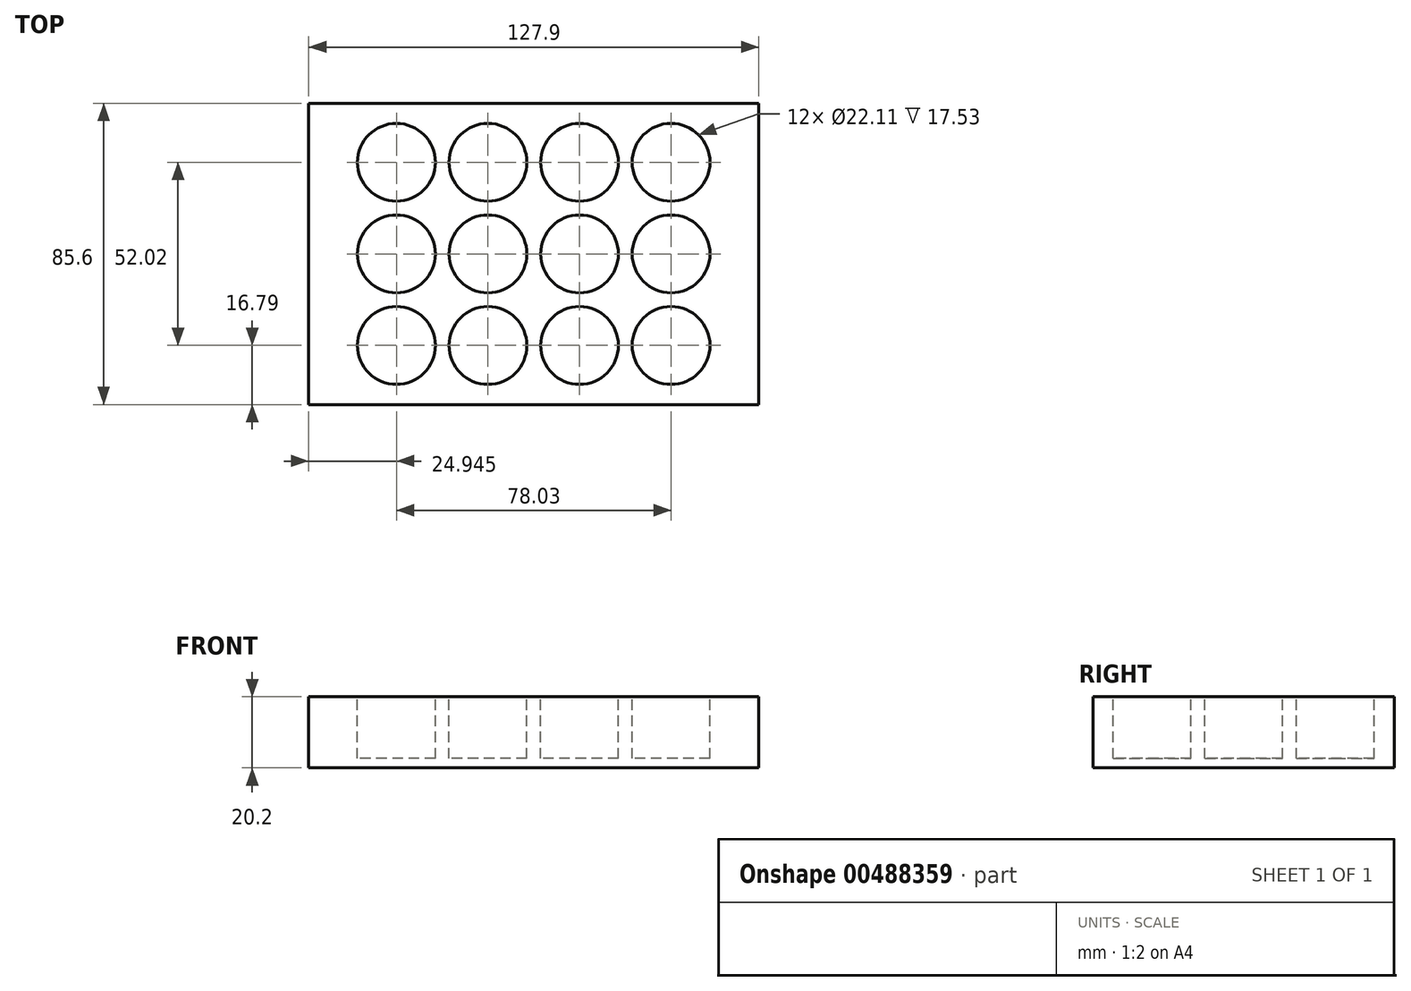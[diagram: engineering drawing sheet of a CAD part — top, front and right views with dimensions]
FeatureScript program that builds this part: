
annotation { "Feature Type Name" : "Feature", "Feature Type Description" : "" }
export const myFeature = defineFeature(function(context is Context, id is Id, definition is map)
    precondition{}
    {
        {
            var Q0;
            Q0=qCreatedBy(makeId("Top.planeOp"),FACE);
            var sketch = newSketch(context, id + "F0", { "sketchPlane" : qUnion([Q0])});
            skLineSegment(sketch, "E0.bottom", {"start": v(63.95, 42.8) * mm, "end": v(-63.95, 42.8) * mm});
            skLineSegment(sketch, "E0.top", {"start": v(63.95, -42.8) * mm, "end": v(-63.95, -42.8) * mm});
            skLineSegment(sketch, "E0.left", {"start": v(63.95, 42.8) * mm, "end": v(63.95, -42.8) * mm});
            skLineSegment(sketch, "E0.right", {"start": v(-63.95, 42.8) * mm, "end": v(-63.95, -42.8) * mm});
            skPoint(sketch, "E0.middle", {"position": v(0, 0) * mm});
            skSolve(sketch);
        }
        {
            var Q0;
            Q0=qSketchRegion(id+"F0",true);
            extrude(context, id + "F1", {"entities" : qUnion([Q0]), "depth" : 20.2 * mm});
        }
        {
            var Q0;
            Q0=makeQuery(id+"F1.opExtrude","CAP_FACE",FACE,{"disambiguationData":[OSD([sQuery(id+"F0.wireOp",EDGE,"E0.bottom"),sQuery(id+"F0.wireOp",EDGE,"E0.top"),sQuery(id+"F0.wireOp",EDGE,"E0.left"),sQuery(id+"F0.wireOp",EDGE,"E0.right")])],"isStart":false});
            var sketch = newSketch(context, id + "F2", { "sketchPlane" : qUnion([Q0])});
            skLineSegment(sketch, "E1.bottom", {"start": v(63.95, 42.8) * mm, "end": v(-63.95, 42.8) * mm});
            skLineSegment(sketch, "E1.top", {"start": v(63.95, -42.8) * mm, "end": v(-63.95, -42.8) * mm});
            skLineSegment(sketch, "E1.left", {"start": v(63.95, 42.8) * mm, "end": v(63.95, -42.8) * mm});
            skLineSegment(sketch, "E1.right", {"start": v(-63.95, 42.8) * mm, "end": v(-63.95, -42.8) * mm});
            skPoint(sketch, "E1.middle", {"position": v(0, 0) * mm});
            skLineSegment(sketch, "E2", {"start": v(-63.95, -42.8) * mm, "end": v(-39, -42.8) * mm});
            skLineSegment(sketch, "E3", {"start": v(-63.95, 42.8) * mm, "end": v(-63.95, 26) * mm});
            skLineSegment(sketch, "E4", {"start": v(-39, -42.8) * mm, "end": v(-13, -42.8) * mm});
            skLineSegment(sketch, "E5", {"start": v(-13, -42.8) * mm, "end": v(13.01, -42.8) * mm});
            skLineSegment(sketch, "E6", {"start": v(13.01, -42.8) * mm, "end": v(39.02, -42.8) * mm});
            skLineSegment(sketch, "E7", {"start": v(-63.95, 26) * mm, "end": v(-63.95, 0) * mm});
            skLineSegment(sketch, "E8", {"start": v(-63.95, 0) * mm, "end": v(-63.95, -26.01) * mm});
            skLineSegment(sketch, "E9", {"start": v(-63.95, 26) * mm, "end": v(63.95, 26.01) * mm});
            skLineSegment(sketch, "E10", {"start": v(63.95, 26.01) * mm, "end": v(63.95, 42.8) * mm});
            skLineSegment(sketch, "E11", {"start": v(-63.95, 0) * mm, "end": v(63.95, 0) * mm});
            skLineSegment(sketch, "E12", {"start": v(63.95, 0) * mm, "end": v(63.95, 26.01) * mm});
            skLineSegment(sketch, "E13", {"start": v(-63.95, -26.01) * mm, "end": v(63.95, -26.01) * mm});
            skLineSegment(sketch, "E14", {"start": v(63.95, -26.01) * mm, "end": v(63.95, 0) * mm});
            skLineSegment(sketch, "E15", {"start": v(-39, -42.8) * mm, "end": v(-39, 42.8) * mm});
            skLineSegment(sketch, "E16", {"start": v(-39, 42.8) * mm, "end": v(-63.95, 42.8) * mm});
            skLineSegment(sketch, "E17", {"start": v(-13, -42.8) * mm, "end": v(-13, 42.8) * mm});
            skLineSegment(sketch, "E18", {"start": v(-13, 42.8) * mm, "end": v(-39, 42.8) * mm});
            skLineSegment(sketch, "E19", {"start": v(13.01, -42.8) * mm, "end": v(13.01, 42.8) * mm});
            skLineSegment(sketch, "E20", {"start": v(13.01, 42.8) * mm, "end": v(-13, 42.8) * mm});
            skLineSegment(sketch, "E21", {"start": v(39.02, -42.8) * mm, "end": v(39.02, 42.8) * mm});
            skLineSegment(sketch, "E22", {"start": v(39.02, 42.8) * mm, "end": v(13.01, 42.8) * mm});
            skCircle(sketch, "E23", {"center": v(-39, 26) * mm, "radius": 11.05 * mm});
            skCircle(sketch, "E24", {"center": v(-13, 26) * mm, "radius": 11.05 * mm});
            skCircle(sketch, "E25", {"center": v(13.01, 26) * mm, "radius": 11.05 * mm});
            skCircle(sketch, "E26", {"center": v(39.02, 26.01) * mm, "radius": 11.05 * mm});
            skCircle(sketch, "E27", {"center": v(-13, 0) * mm, "radius": 11.05 * mm});
            skCircle(sketch, "E28", {"center": v(13.01, 0) * mm, "radius": 11.05 * mm});
            skCircle(sketch, "E29", {"center": v(39.02, 0) * mm, "radius": 11.05 * mm});
            skCircle(sketch, "E30", {"center": v(-13, -26.01) * mm, "radius": 11.05 * mm});
            skCircle(sketch, "E31", {"center": v(13.01, -26.01) * mm, "radius": 11.05 * mm});
            skCircle(sketch, "E32", {"center": v(39.02, -26.01) * mm, "radius": 11.05 * mm});
            skCircle(sketch, "E33", {"center": v(-39, 0) * mm, "radius": 11.05 * mm});
            skCircle(sketch, "E34", {"center": v(-39, -26.01) * mm, "radius": 11.05 * mm});
            skLineSegment(sketch, "E35", {"start": v(39.02, -42.8) * mm, "end": v(63.95, -42.8) * mm});
            skLineSegment(sketch, "E36", {"start": v(63.95, -26.01) * mm, "end": v(63.95, -42.8) * mm});
            skSolve(sketch);
        }
        {
            var Q0;
            {var subQ0=sQuery(id+"F2.wireOp",EDGE,"E23");var subQ1=sQuery(id+"F2.wireOp",EDGE,"E9");var subQ2=makeQuery(id+"F2.imprint","INTERSECT",VERTEX,{"disambiguationData":[OD(0.0)],"derivedFrom":[subQ1,subQ0]});Q0=makeQuery(id+"F2.imprint","IMPRINT",FACE,{"disambiguationData":[TD([[makeQuery(id+"F2.imprint","IMPRINT",EDGE,{"disambiguationData":[TD([[subQ2,-1.0]])],"derivedFrom":subQ1}),1.0]])]});}
            var Q1;
            {var subQ0=sQuery(id+"F2.wireOp",EDGE,"E15");var subQ1=sQuery(id+"F2.wireOp",EDGE,"E9");var subQ2=makeQuery(id+"F2.imprint","INTERSECT",VERTEX,{"derivedFrom":[subQ1,subQ0]});Q1=makeQuery(id+"F2.imprint","IMPRINT",FACE,{"disambiguationData":[TD([[makeQuery(id+"F2.imprint","IMPRINT",EDGE,{"disambiguationData":[TD([[subQ2,-1.0]])],"derivedFrom":subQ1}),1.0]])]});}
            var Q2;
            {var subQ0=sQuery(id+"F2.wireOp",EDGE,"E15");var subQ1=sQuery(id+"F2.wireOp",EDGE,"E9");var subQ2=makeQuery(id+"F2.imprint","INTERSECT",VERTEX,{"derivedFrom":[subQ1,subQ0]});Q2=makeQuery(id+"F2.imprint","IMPRINT",FACE,{"disambiguationData":[TD([[makeQuery(id+"F2.imprint","IMPRINT",EDGE,{"disambiguationData":[TD([[subQ2,-1.0]])],"derivedFrom":subQ1}),-1.0]])]});}
            var Q3;
            {var subQ0=sQuery(id+"F2.wireOp",EDGE,"E23");var subQ1=sQuery(id+"F2.wireOp",EDGE,"E9");var subQ2=makeQuery(id+"F2.imprint","INTERSECT",VERTEX,{"disambiguationData":[OD(0.0)],"derivedFrom":[subQ1,subQ0]});Q3=makeQuery(id+"F2.imprint","IMPRINT",FACE,{"disambiguationData":[TD([[makeQuery(id+"F2.imprint","IMPRINT",EDGE,{"disambiguationData":[TD([[subQ2,-1.0]])],"derivedFrom":subQ1}),-1.0]])]});}
            var Q4;
            {var subQ0=sQuery(id+"F2.wireOp",EDGE,"E33");var subQ1=sQuery(id+"F2.wireOp",EDGE,"E11");var subQ2=makeQuery(id+"F2.imprint","INTERSECT",VERTEX,{"disambiguationData":[OD(0.0)],"derivedFrom":[subQ1,subQ0]});Q4=makeQuery(id+"F2.imprint","IMPRINT",FACE,{"disambiguationData":[TD([[makeQuery(id+"F2.imprint","IMPRINT",EDGE,{"disambiguationData":[TD([[subQ2,-1.0]])],"derivedFrom":subQ1}),1.0]])]});}
            var Q5;
            {var subQ0=sQuery(id+"F2.wireOp",EDGE,"E15");var subQ1=sQuery(id+"F2.wireOp",EDGE,"E11");var subQ2=makeQuery(id+"F2.imprint","INTERSECT",VERTEX,{"derivedFrom":[subQ1,subQ0]});Q5=makeQuery(id+"F2.imprint","IMPRINT",FACE,{"disambiguationData":[TD([[makeQuery(id+"F2.imprint","IMPRINT",EDGE,{"disambiguationData":[TD([[subQ2,-1.0]])],"derivedFrom":subQ1}),1.0]])]});}
            var Q6;
            {var subQ0=sQuery(id+"F2.wireOp",EDGE,"E33");var subQ1=sQuery(id+"F2.wireOp",EDGE,"E11");var subQ2=makeQuery(id+"F2.imprint","INTERSECT",VERTEX,{"disambiguationData":[OD(0.0)],"derivedFrom":[subQ1,subQ0]});Q6=makeQuery(id+"F2.imprint","IMPRINT",FACE,{"disambiguationData":[TD([[makeQuery(id+"F2.imprint","IMPRINT",EDGE,{"disambiguationData":[TD([[subQ2,-1.0]])],"derivedFrom":subQ1}),-1.0]])]});}
            var Q7;
            {var subQ0=sQuery(id+"F2.wireOp",EDGE,"E15");var subQ1=sQuery(id+"F2.wireOp",EDGE,"E11");var subQ2=makeQuery(id+"F2.imprint","INTERSECT",VERTEX,{"derivedFrom":[subQ1,subQ0]});Q7=makeQuery(id+"F2.imprint","IMPRINT",FACE,{"disambiguationData":[TD([[makeQuery(id+"F2.imprint","IMPRINT",EDGE,{"disambiguationData":[TD([[subQ2,-1.0]])],"derivedFrom":subQ1}),-1.0]])]});}
            var Q8;
            {var subQ0=sQuery(id+"F2.wireOp",EDGE,"E15");var subQ1=sQuery(id+"F2.wireOp",EDGE,"E13");var subQ2=makeQuery(id+"F2.imprint","INTERSECT",VERTEX,{"derivedFrom":[subQ1,subQ0]});Q8=makeQuery(id+"F2.imprint","IMPRINT",FACE,{"disambiguationData":[TD([[makeQuery(id+"F2.imprint","IMPRINT",EDGE,{"disambiguationData":[TD([[subQ2,-1.0]])],"derivedFrom":subQ1}),1.0]])]});}
            var Q9;
            {var subQ0=sQuery(id+"F2.wireOp",EDGE,"E34");var subQ1=sQuery(id+"F2.wireOp",EDGE,"E13");var subQ2=makeQuery(id+"F2.imprint","INTERSECT",VERTEX,{"disambiguationData":[OD(0.0)],"derivedFrom":[subQ1,subQ0]});Q9=makeQuery(id+"F2.imprint","IMPRINT",FACE,{"disambiguationData":[TD([[makeQuery(id+"F2.imprint","IMPRINT",EDGE,{"disambiguationData":[TD([[subQ2,-1.0]])],"derivedFrom":subQ1}),1.0]])]});}
            var Q10;
            {var subQ0=sQuery(id+"F2.wireOp",EDGE,"E34");var subQ1=sQuery(id+"F2.wireOp",EDGE,"E13");var subQ2=makeQuery(id+"F2.imprint","INTERSECT",VERTEX,{"disambiguationData":[OD(0.0)],"derivedFrom":[subQ1,subQ0]});Q10=makeQuery(id+"F2.imprint","IMPRINT",FACE,{"disambiguationData":[TD([[makeQuery(id+"F2.imprint","IMPRINT",EDGE,{"disambiguationData":[TD([[subQ2,-1.0]])],"derivedFrom":subQ1}),-1.0]])]});}
            var Q11;
            {var subQ0=sQuery(id+"F2.wireOp",EDGE,"E15");var subQ1=sQuery(id+"F2.wireOp",EDGE,"E13");var subQ2=makeQuery(id+"F2.imprint","INTERSECT",VERTEX,{"derivedFrom":[subQ1,subQ0]});Q11=makeQuery(id+"F2.imprint","IMPRINT",FACE,{"disambiguationData":[TD([[makeQuery(id+"F2.imprint","IMPRINT",EDGE,{"disambiguationData":[TD([[subQ2,-1.0]])],"derivedFrom":subQ1}),-1.0]])]});}
            var Q12;
            {var subQ0=sQuery(id+"F2.wireOp",EDGE,"E30");var subQ1=sQuery(id+"F2.wireOp",EDGE,"E13");var subQ2=makeQuery(id+"F2.imprint","INTERSECT",VERTEX,{"disambiguationData":[OD(0.0)],"derivedFrom":[subQ1,subQ0]});Q12=makeQuery(id+"F2.imprint","IMPRINT",FACE,{"disambiguationData":[TD([[makeQuery(id+"F2.imprint","IMPRINT",EDGE,{"disambiguationData":[TD([[subQ2,-1.0]])],"derivedFrom":subQ1}),-1.0]])]});}
            var Q13;
            {var subQ0=sQuery(id+"F2.wireOp",EDGE,"E17");var subQ1=sQuery(id+"F2.wireOp",EDGE,"E13");var subQ2=makeQuery(id+"F2.imprint","INTERSECT",VERTEX,{"derivedFrom":[subQ1,subQ0]});Q13=makeQuery(id+"F2.imprint","IMPRINT",FACE,{"disambiguationData":[TD([[makeQuery(id+"F2.imprint","IMPRINT",EDGE,{"disambiguationData":[TD([[subQ2,-1.0]])],"derivedFrom":subQ1}),-1.0]])]});}
            var Q14;
            {var subQ0=sQuery(id+"F2.wireOp",EDGE,"E17");var subQ1=sQuery(id+"F2.wireOp",EDGE,"E13");var subQ2=makeQuery(id+"F2.imprint","INTERSECT",VERTEX,{"derivedFrom":[subQ1,subQ0]});Q14=makeQuery(id+"F2.imprint","IMPRINT",FACE,{"disambiguationData":[TD([[makeQuery(id+"F2.imprint","IMPRINT",EDGE,{"disambiguationData":[TD([[subQ2,-1.0]])],"derivedFrom":subQ1}),1.0]])]});}
            var Q15;
            {var subQ0=sQuery(id+"F2.wireOp",EDGE,"E30");var subQ1=sQuery(id+"F2.wireOp",EDGE,"E13");var subQ2=makeQuery(id+"F2.imprint","INTERSECT",VERTEX,{"disambiguationData":[OD(0.0)],"derivedFrom":[subQ1,subQ0]});Q15=makeQuery(id+"F2.imprint","IMPRINT",FACE,{"disambiguationData":[TD([[makeQuery(id+"F2.imprint","IMPRINT",EDGE,{"disambiguationData":[TD([[subQ2,-1.0]])],"derivedFrom":subQ1}),1.0]])]});}
            var Q16;
            {var subQ0=sQuery(id+"F2.wireOp",EDGE,"E27");var subQ1=sQuery(id+"F2.wireOp",EDGE,"E11");var subQ2=makeQuery(id+"F2.imprint","INTERSECT",VERTEX,{"disambiguationData":[OD(0.0)],"derivedFrom":[subQ1,subQ0]});Q16=makeQuery(id+"F2.imprint","IMPRINT",FACE,{"disambiguationData":[TD([[makeQuery(id+"F2.imprint","IMPRINT",EDGE,{"disambiguationData":[TD([[subQ2,-1.0]])],"derivedFrom":subQ1}),-1.0]])]});}
            var Q17;
            {var subQ0=sQuery(id+"F2.wireOp",EDGE,"E17");var subQ1=sQuery(id+"F2.wireOp",EDGE,"E11");var subQ2=makeQuery(id+"F2.imprint","INTERSECT",VERTEX,{"derivedFrom":[subQ1,subQ0]});Q17=makeQuery(id+"F2.imprint","IMPRINT",FACE,{"disambiguationData":[TD([[makeQuery(id+"F2.imprint","IMPRINT",EDGE,{"disambiguationData":[TD([[subQ2,-1.0]])],"derivedFrom":subQ1}),-1.0]])]});}
            var Q18;
            {var subQ0=sQuery(id+"F2.wireOp",EDGE,"E17");var subQ1=sQuery(id+"F2.wireOp",EDGE,"E11");var subQ2=makeQuery(id+"F2.imprint","INTERSECT",VERTEX,{"derivedFrom":[subQ1,subQ0]});Q18=makeQuery(id+"F2.imprint","IMPRINT",FACE,{"disambiguationData":[TD([[makeQuery(id+"F2.imprint","IMPRINT",EDGE,{"disambiguationData":[TD([[subQ2,-1.0]])],"derivedFrom":subQ1}),1.0]])]});}
            var Q19;
            {var subQ0=sQuery(id+"F2.wireOp",EDGE,"E27");var subQ1=sQuery(id+"F2.wireOp",EDGE,"E11");var subQ2=makeQuery(id+"F2.imprint","INTERSECT",VERTEX,{"disambiguationData":[OD(0.0)],"derivedFrom":[subQ1,subQ0]});Q19=makeQuery(id+"F2.imprint","IMPRINT",FACE,{"disambiguationData":[TD([[makeQuery(id+"F2.imprint","IMPRINT",EDGE,{"disambiguationData":[TD([[subQ2,-1.0]])],"derivedFrom":subQ1}),1.0]])]});}
            var Q20;
            {var subQ0=sQuery(id+"F2.wireOp",EDGE,"E24");var subQ1=sQuery(id+"F2.wireOp",EDGE,"E9");var subQ2=makeQuery(id+"F2.imprint","INTERSECT",VERTEX,{"disambiguationData":[OD(0.0)],"derivedFrom":[subQ1,subQ0]});Q20=makeQuery(id+"F2.imprint","IMPRINT",FACE,{"disambiguationData":[TD([[makeQuery(id+"F2.imprint","IMPRINT",EDGE,{"disambiguationData":[TD([[subQ2,-1.0]])],"derivedFrom":subQ1}),-1.0]])]});}
            var Q21;
            {var subQ0=sQuery(id+"F2.wireOp",EDGE,"E17");var subQ1=sQuery(id+"F2.wireOp",EDGE,"E9");var subQ2=makeQuery(id+"F2.imprint","INTERSECT",VERTEX,{"derivedFrom":[subQ1,subQ0]});Q21=makeQuery(id+"F2.imprint","IMPRINT",FACE,{"disambiguationData":[TD([[makeQuery(id+"F2.imprint","IMPRINT",EDGE,{"disambiguationData":[TD([[subQ2,-1.0]])],"derivedFrom":subQ1}),-1.0]])]});}
            var Q22;
            {var subQ0=sQuery(id+"F2.wireOp",EDGE,"E17");var subQ1=sQuery(id+"F2.wireOp",EDGE,"E9");var subQ2=makeQuery(id+"F2.imprint","INTERSECT",VERTEX,{"derivedFrom":[subQ1,subQ0]});Q22=makeQuery(id+"F2.imprint","IMPRINT",FACE,{"disambiguationData":[TD([[makeQuery(id+"F2.imprint","IMPRINT",EDGE,{"disambiguationData":[TD([[subQ2,-1.0]])],"derivedFrom":subQ1}),1.0]])]});}
            var Q23;
            {var subQ0=sQuery(id+"F2.wireOp",EDGE,"E24");var subQ1=sQuery(id+"F2.wireOp",EDGE,"E9");var subQ2=makeQuery(id+"F2.imprint","INTERSECT",VERTEX,{"disambiguationData":[OD(0.0)],"derivedFrom":[subQ1,subQ0]});Q23=makeQuery(id+"F2.imprint","IMPRINT",FACE,{"disambiguationData":[TD([[makeQuery(id+"F2.imprint","IMPRINT",EDGE,{"disambiguationData":[TD([[subQ2,-1.0]])],"derivedFrom":subQ1}),1.0]])]});}
            var Q24;
            {var subQ0=sQuery(id+"F2.wireOp",EDGE,"E25");var subQ1=sQuery(id+"F2.wireOp",EDGE,"E9");var subQ2=makeQuery(id+"F2.imprint","INTERSECT",VERTEX,{"disambiguationData":[OD(0.0)],"derivedFrom":[subQ1,subQ0]});Q24=makeQuery(id+"F2.imprint","IMPRINT",FACE,{"disambiguationData":[TD([[makeQuery(id+"F2.imprint","IMPRINT",EDGE,{"disambiguationData":[TD([[subQ2,-1.0]])],"derivedFrom":subQ1}),1.0]])]});}
            var Q25;
            {var subQ0=sQuery(id+"F2.wireOp",EDGE,"E19");var subQ1=sQuery(id+"F2.wireOp",EDGE,"E9");var subQ2=makeQuery(id+"F2.imprint","INTERSECT",VERTEX,{"derivedFrom":[subQ1,subQ0]});Q25=makeQuery(id+"F2.imprint","IMPRINT",FACE,{"disambiguationData":[TD([[makeQuery(id+"F2.imprint","IMPRINT",EDGE,{"disambiguationData":[TD([[subQ2,-1.0]])],"derivedFrom":subQ1}),1.0]])]});}
            var Q26;
            {var subQ0=sQuery(id+"F2.wireOp",EDGE,"E19");var subQ1=sQuery(id+"F2.wireOp",EDGE,"E9");var subQ2=makeQuery(id+"F2.imprint","INTERSECT",VERTEX,{"derivedFrom":[subQ1,subQ0]});Q26=makeQuery(id+"F2.imprint","IMPRINT",FACE,{"disambiguationData":[TD([[makeQuery(id+"F2.imprint","IMPRINT",EDGE,{"disambiguationData":[TD([[subQ2,-1.0]])],"derivedFrom":subQ1}),-1.0]])]});}
            var Q27;
            {var subQ0=sQuery(id+"F2.wireOp",EDGE,"E25");var subQ1=sQuery(id+"F2.wireOp",EDGE,"E9");var subQ2=makeQuery(id+"F2.imprint","INTERSECT",VERTEX,{"disambiguationData":[OD(0.0)],"derivedFrom":[subQ1,subQ0]});Q27=makeQuery(id+"F2.imprint","IMPRINT",FACE,{"disambiguationData":[TD([[makeQuery(id+"F2.imprint","IMPRINT",EDGE,{"disambiguationData":[TD([[subQ2,-1.0]])],"derivedFrom":subQ1}),-1.0]])]});}
            var Q28;
            {var subQ0=sQuery(id+"F2.wireOp",EDGE,"E28");var subQ1=sQuery(id+"F2.wireOp",EDGE,"E11");var subQ2=makeQuery(id+"F2.imprint","INTERSECT",VERTEX,{"disambiguationData":[OD(0.0)],"derivedFrom":[subQ1,subQ0]});Q28=makeQuery(id+"F2.imprint","IMPRINT",FACE,{"disambiguationData":[TD([[makeQuery(id+"F2.imprint","IMPRINT",EDGE,{"disambiguationData":[TD([[subQ2,-1.0]])],"derivedFrom":subQ1}),1.0]])]});}
            var Q29;
            {var subQ0=sQuery(id+"F2.wireOp",EDGE,"E19");var subQ1=sQuery(id+"F2.wireOp",EDGE,"E11");var subQ2=makeQuery(id+"F2.imprint","INTERSECT",VERTEX,{"derivedFrom":[subQ1,subQ0]});Q29=makeQuery(id+"F2.imprint","IMPRINT",FACE,{"disambiguationData":[TD([[makeQuery(id+"F2.imprint","IMPRINT",EDGE,{"disambiguationData":[TD([[subQ2,-1.0]])],"derivedFrom":subQ1}),1.0]])]});}
            var Q30;
            {var subQ0=sQuery(id+"F2.wireOp",EDGE,"E28");var subQ1=sQuery(id+"F2.wireOp",EDGE,"E11");var subQ2=makeQuery(id+"F2.imprint","INTERSECT",VERTEX,{"disambiguationData":[OD(0.0)],"derivedFrom":[subQ1,subQ0]});Q30=makeQuery(id+"F2.imprint","IMPRINT",FACE,{"disambiguationData":[TD([[makeQuery(id+"F2.imprint","IMPRINT",EDGE,{"disambiguationData":[TD([[subQ2,-1.0]])],"derivedFrom":subQ1}),-1.0]])]});}
            var Q31;
            {var subQ0=sQuery(id+"F2.wireOp",EDGE,"E19");var subQ1=sQuery(id+"F2.wireOp",EDGE,"E11");var subQ2=makeQuery(id+"F2.imprint","INTERSECT",VERTEX,{"derivedFrom":[subQ1,subQ0]});Q31=makeQuery(id+"F2.imprint","IMPRINT",FACE,{"disambiguationData":[TD([[makeQuery(id+"F2.imprint","IMPRINT",EDGE,{"disambiguationData":[TD([[subQ2,-1.0]])],"derivedFrom":subQ1}),-1.0]])]});}
            var Q32;
            {var subQ0=sQuery(id+"F2.wireOp",EDGE,"E29");var subQ1=sQuery(id+"F2.wireOp",EDGE,"E11");var subQ2=makeQuery(id+"F2.imprint","INTERSECT",VERTEX,{"disambiguationData":[OD(0.0)],"derivedFrom":[subQ1,subQ0]});Q32=makeQuery(id+"F2.imprint","IMPRINT",FACE,{"disambiguationData":[TD([[makeQuery(id+"F2.imprint","IMPRINT",EDGE,{"disambiguationData":[TD([[subQ2,-1.0]])],"derivedFrom":subQ1}),-1.0]])]});}
            var Q33;
            {var subQ0=sQuery(id+"F2.wireOp",EDGE,"E21");var subQ1=sQuery(id+"F2.wireOp",EDGE,"E11");var subQ2=makeQuery(id+"F2.imprint","INTERSECT",VERTEX,{"derivedFrom":[subQ1,subQ0]});Q33=makeQuery(id+"F2.imprint","IMPRINT",FACE,{"disambiguationData":[TD([[makeQuery(id+"F2.imprint","IMPRINT",EDGE,{"disambiguationData":[TD([[subQ2,-1.0]])],"derivedFrom":subQ1}),-1.0]])]});}
            var Q34;
            {var subQ0=sQuery(id+"F2.wireOp",EDGE,"E21");var subQ1=sQuery(id+"F2.wireOp",EDGE,"E11");var subQ2=makeQuery(id+"F2.imprint","INTERSECT",VERTEX,{"derivedFrom":[subQ1,subQ0]});Q34=makeQuery(id+"F2.imprint","IMPRINT",FACE,{"disambiguationData":[TD([[makeQuery(id+"F2.imprint","IMPRINT",EDGE,{"disambiguationData":[TD([[subQ2,-1.0]])],"derivedFrom":subQ1}),1.0]])]});}
            var Q35;
            {var subQ0=sQuery(id+"F2.wireOp",EDGE,"E29");var subQ1=sQuery(id+"F2.wireOp",EDGE,"E11");var subQ2=makeQuery(id+"F2.imprint","INTERSECT",VERTEX,{"disambiguationData":[OD(0.0)],"derivedFrom":[subQ1,subQ0]});Q35=makeQuery(id+"F2.imprint","IMPRINT",FACE,{"disambiguationData":[TD([[makeQuery(id+"F2.imprint","IMPRINT",EDGE,{"disambiguationData":[TD([[subQ2,-1.0]])],"derivedFrom":subQ1}),1.0]])]});}
            var Q36;
            {var subQ0=sQuery(id+"F2.wireOp",EDGE,"E26");var subQ1=sQuery(id+"F2.wireOp",EDGE,"E9");var subQ2=makeQuery(id+"F2.imprint","INTERSECT",VERTEX,{"disambiguationData":[OD(0.0)],"derivedFrom":[subQ1,subQ0]});Q36=makeQuery(id+"F2.imprint","IMPRINT",FACE,{"disambiguationData":[TD([[makeQuery(id+"F2.imprint","IMPRINT",EDGE,{"disambiguationData":[TD([[subQ2,-1.0]])],"derivedFrom":subQ1}),-1.0]])]});}
            var Q37;
            {var subQ0=sQuery(id+"F2.wireOp",EDGE,"E21");var subQ1=sQuery(id+"F2.wireOp",EDGE,"E9");var subQ2=makeQuery(id+"F2.imprint","INTERSECT",VERTEX,{"derivedFrom":[subQ1,subQ0]});Q37=makeQuery(id+"F2.imprint","IMPRINT",FACE,{"disambiguationData":[TD([[makeQuery(id+"F2.imprint","IMPRINT",EDGE,{"disambiguationData":[TD([[subQ2,-1.0]])],"derivedFrom":subQ1}),-1.0]])]});}
            var Q38;
            {var subQ0=sQuery(id+"F2.wireOp",EDGE,"E21");var subQ1=sQuery(id+"F2.wireOp",EDGE,"E9");var subQ2=makeQuery(id+"F2.imprint","INTERSECT",VERTEX,{"derivedFrom":[subQ1,subQ0]});Q38=makeQuery(id+"F2.imprint","IMPRINT",FACE,{"disambiguationData":[TD([[makeQuery(id+"F2.imprint","IMPRINT",EDGE,{"disambiguationData":[TD([[subQ2,-1.0]])],"derivedFrom":subQ1}),1.0]])]});}
            var Q39;
            {var subQ0=sQuery(id+"F2.wireOp",EDGE,"E26");var subQ1=sQuery(id+"F2.wireOp",EDGE,"E9");var subQ2=makeQuery(id+"F2.imprint","INTERSECT",VERTEX,{"disambiguationData":[OD(0.0)],"derivedFrom":[subQ1,subQ0]});Q39=makeQuery(id+"F2.imprint","IMPRINT",FACE,{"disambiguationData":[TD([[makeQuery(id+"F2.imprint","IMPRINT",EDGE,{"disambiguationData":[TD([[subQ2,-1.0]])],"derivedFrom":subQ1}),1.0]])]});}
            var Q40;
            {var subQ0=sQuery(id+"F2.wireOp",EDGE,"E19");var subQ1=sQuery(id+"F2.wireOp",EDGE,"E13");var subQ2=makeQuery(id+"F2.imprint","INTERSECT",VERTEX,{"derivedFrom":[subQ1,subQ0]});Q40=makeQuery(id+"F2.imprint","IMPRINT",FACE,{"disambiguationData":[TD([[makeQuery(id+"F2.imprint","IMPRINT",EDGE,{"disambiguationData":[TD([[subQ2,-1.0]])],"derivedFrom":subQ1}),1.0]])]});}
            var Q41;
            {var subQ0=sQuery(id+"F2.wireOp",EDGE,"E31");var subQ1=sQuery(id+"F2.wireOp",EDGE,"E13");var subQ2=makeQuery(id+"F2.imprint","INTERSECT",VERTEX,{"disambiguationData":[OD(0.0)],"derivedFrom":[subQ1,subQ0]});Q41=makeQuery(id+"F2.imprint","IMPRINT",FACE,{"disambiguationData":[TD([[makeQuery(id+"F2.imprint","IMPRINT",EDGE,{"disambiguationData":[TD([[subQ2,-1.0]])],"derivedFrom":subQ1}),1.0]])]});}
            var Q42;
            {var subQ0=sQuery(id+"F2.wireOp",EDGE,"E31");var subQ1=sQuery(id+"F2.wireOp",EDGE,"E13");var subQ2=makeQuery(id+"F2.imprint","INTERSECT",VERTEX,{"disambiguationData":[OD(0.0)],"derivedFrom":[subQ1,subQ0]});Q42=makeQuery(id+"F2.imprint","IMPRINT",FACE,{"disambiguationData":[TD([[makeQuery(id+"F2.imprint","IMPRINT",EDGE,{"disambiguationData":[TD([[subQ2,-1.0]])],"derivedFrom":subQ1}),-1.0]])]});}
            var Q43;
            {var subQ0=sQuery(id+"F2.wireOp",EDGE,"E19");var subQ1=sQuery(id+"F2.wireOp",EDGE,"E13");var subQ2=makeQuery(id+"F2.imprint","INTERSECT",VERTEX,{"derivedFrom":[subQ1,subQ0]});Q43=makeQuery(id+"F2.imprint","IMPRINT",FACE,{"disambiguationData":[TD([[makeQuery(id+"F2.imprint","IMPRINT",EDGE,{"disambiguationData":[TD([[subQ2,-1.0]])],"derivedFrom":subQ1}),-1.0]])]});}
            var Q44;
            {var subQ0=sQuery(id+"F2.wireOp",EDGE,"E32");var subQ1=sQuery(id+"F2.wireOp",EDGE,"E13");var subQ2=makeQuery(id+"F2.imprint","INTERSECT",VERTEX,{"disambiguationData":[OD(0.0)],"derivedFrom":[subQ1,subQ0]});Q44=makeQuery(id+"F2.imprint","IMPRINT",FACE,{"disambiguationData":[TD([[makeQuery(id+"F2.imprint","IMPRINT",EDGE,{"disambiguationData":[TD([[subQ2,-1.0]])],"derivedFrom":subQ1}),1.0]])]});}
            var Q45;
            {var subQ0=sQuery(id+"F2.wireOp",EDGE,"E21");var subQ1=sQuery(id+"F2.wireOp",EDGE,"E13");var subQ2=makeQuery(id+"F2.imprint","INTERSECT",VERTEX,{"derivedFrom":[subQ1,subQ0]});Q45=makeQuery(id+"F2.imprint","IMPRINT",FACE,{"disambiguationData":[TD([[makeQuery(id+"F2.imprint","IMPRINT",EDGE,{"disambiguationData":[TD([[subQ2,-1.0]])],"derivedFrom":subQ1}),1.0]])]});}
            var Q46;
            {var subQ0=sQuery(id+"F2.wireOp",EDGE,"E21");var subQ1=sQuery(id+"F2.wireOp",EDGE,"E13");var subQ2=makeQuery(id+"F2.imprint","INTERSECT",VERTEX,{"derivedFrom":[subQ1,subQ0]});Q46=makeQuery(id+"F2.imprint","IMPRINT",FACE,{"disambiguationData":[TD([[makeQuery(id+"F2.imprint","IMPRINT",EDGE,{"disambiguationData":[TD([[subQ2,-1.0]])],"derivedFrom":subQ1}),-1.0]])]});}
            var Q47;
            {var subQ0=sQuery(id+"F2.wireOp",EDGE,"E32");var subQ1=sQuery(id+"F2.wireOp",EDGE,"E13");var subQ2=makeQuery(id+"F2.imprint","INTERSECT",VERTEX,{"disambiguationData":[OD(0.0)],"derivedFrom":[subQ1,subQ0]});Q47=makeQuery(id+"F2.imprint","IMPRINT",FACE,{"disambiguationData":[TD([[makeQuery(id+"F2.imprint","IMPRINT",EDGE,{"disambiguationData":[TD([[subQ2,-1.0]])],"derivedFrom":subQ1}),-1.0]])]});}
            extrude(context, id + "F3", {"entities" : qUnion([Q0, Q1, Q2, Q3, Q4, Q5, Q6, Q7, Q8, Q9, Q10, Q11, Q12, Q13, Q14, Q15, Q16, Q17, Q18, Q19, Q20, Q21, Q22, Q23, Q24, Q25, Q26, Q27, Q28, Q29, Q30, Q31, Q32, Q33, Q34, Q35, Q36, Q37, Q38, Q39, Q40, Q41, Q42, Q43, Q44, Q45, Q46, Q47]), "operationType" : NewBodyOperationType.REMOVE, "oppositeDirection" : true, "depth" : 17.53 * mm});
        }
    });
